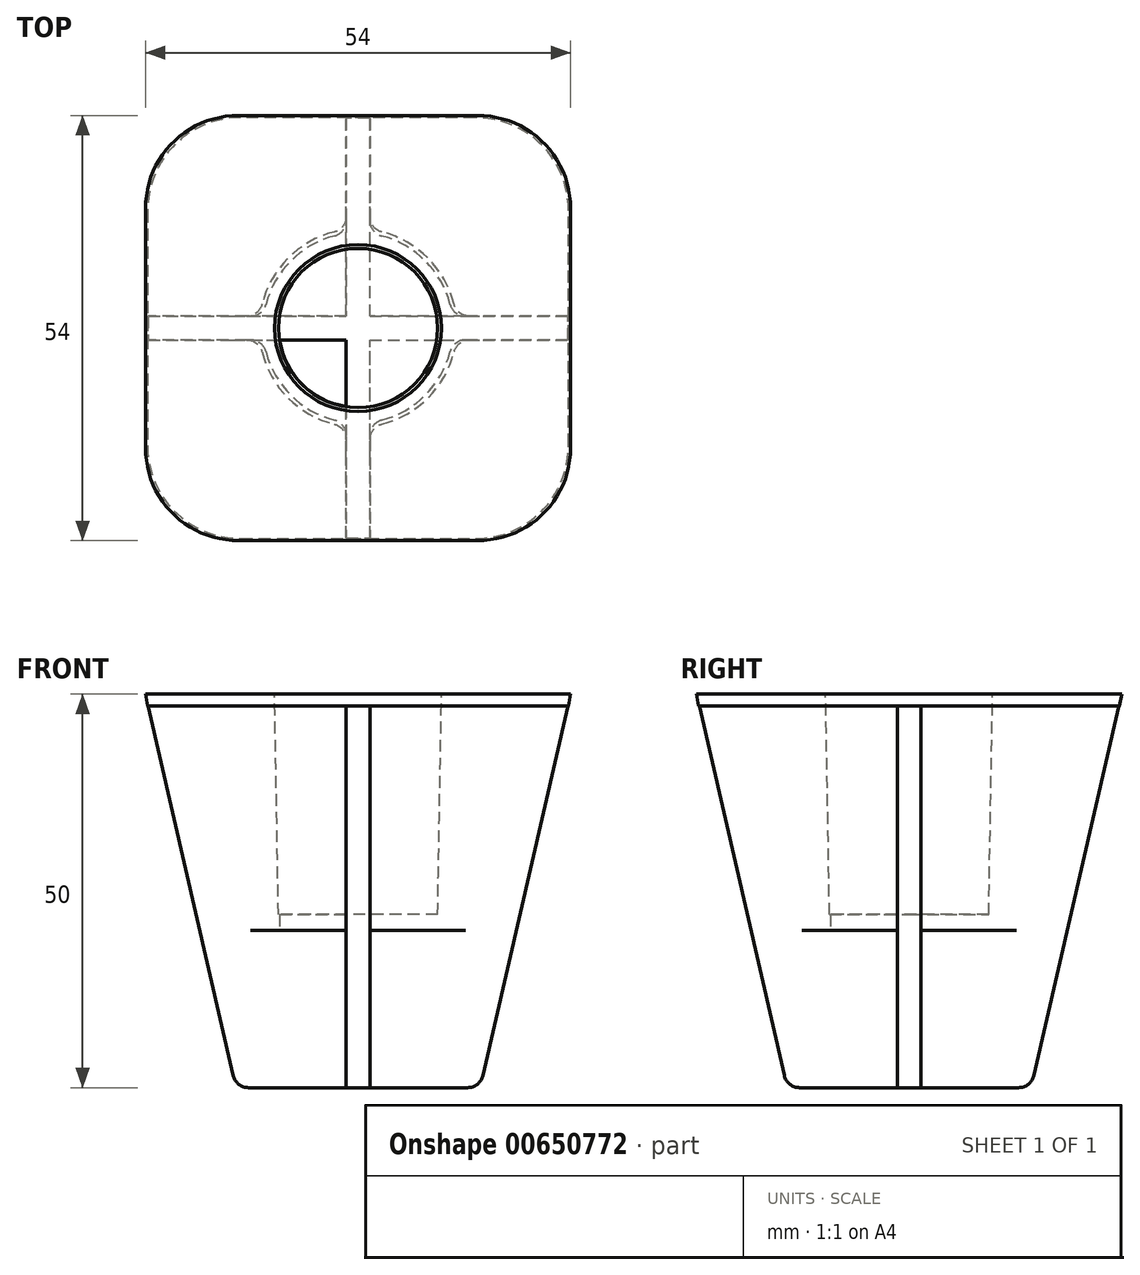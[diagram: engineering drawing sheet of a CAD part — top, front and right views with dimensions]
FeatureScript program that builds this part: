
annotation { "Feature Type Name" : "Feature", "Feature Type Description" : "" }
export const myFeature = defineFeature(function(context is Context, id is Id, definition is map)
    precondition{}
    {
        {
            var Q0;
            Q0=qCreatedBy(makeId("Top.planeOp"),FACE);
            var sketch = newSketch(context, id + "F0", { "sketchPlane" : qUnion([Q0])});
            skCircle(sketch, "E0", {"center": v(0, 0) * mm, "radius": 10.6 * mm});
            skSolve(sketch);
        }
        {
            var Q0;
            Q0 = qSketchRegion(id + "F0", true);
            extrude(context, id + "F1", {"entities" : qUnion([Q0]), "oppositeDirection" : true, "depth" : 28 * mm, "offsetDistance" : 25 * mm, "hasDraft" : true, "draftAngle" : 1 * degree, "draftPullDirection" : true});
        }
        {
            var Q0;
            Q0=makeQuery(id+"F1.opExtrude","CAP_FACE",FACE,{"disambiguationData":[OSD([sQuery(id+"F0.wireOp",EDGE,"E0")])],"isStart":true});
            shell(context, id + "F2", {"entities" : qUnion([Q0]), "thickness" : 2 * mm, "oppositeDirection" : true});
        }
        {
            var Q0;
            Q0=qCreatedBy(makeId("Right.planeOp"),FACE);
            var sketch = newSketch(context, id + "F3", { "sketchPlane" : qUnion([Q0])});
            skLineSegment(sketch, "E1", {"start": v(-10.6, 0) * mm, "end": v(-27, 0) * mm});
            skLineSegment(sketch, "E2", {"start": v(-27, 0) * mm, "end": v(-15.5, -50) * mm});
            skLineSegment(sketch, "E3", {"start": v(-15.5, -50) * mm, "end": v(0, -50) * mm});
            skLineSegment(sketch, "E4", {"start": v(0, -50) * mm, "end": v(15.5, -50) * mm});
            skLineSegment(sketch, "E5", {"start": v(15.5, -50) * mm, "end": v(27, 0) * mm});
            skLineSegment(sketch, "E6", {"start": v(27, 0) * mm, "end": v(10.6, 0) * mm});
            skLineSegment(sketch, "E7", {"start": v(10.6, 0) * mm, "end": v(10.45, -30) * mm});
            skLineSegment(sketch, "E8", {"start": v(10.45, -30) * mm, "end": v(-10.5, -30) * mm});
            skLineSegment(sketch, "E9", {"start": v(-10.5, -30) * mm, "end": v(-10.6, 0) * mm});
            skLineSegment(sketch, "E10.0", {"start": v(-10.6, 0) * mm, "end": v(10.6, 0) * mm, "construction": true});
            skSolve(sketch);
        }
        {
            var Q0;
            Q0 = qSketchRegion(id + "F3", true);
            extrude(context, id + "F4", {"entities" : qUnion([Q0]), "operationType" : NewBodyOperationType.ADD, "depth" : 1.5 * mm, "offsetDistance" : 25 * mm, "hasSecondDirection" : true, "secondDirectionOppositeDirection" : true, "secondDirectionDepth" : 1.5 * mm});
        }
        {
            var Q0;
            Q0=makeQuery(id+"F1.opExtrude","SWEPT_BODY",BODY,{"disambiguationData":[OSD([sQuery(id+"F0.wireOp",EDGE,"E0")])]});
            var Q1;
            {var subQ0=sQuery(id+"F0.wireOp",EDGE,"E0");Q1=makeQuery(id+"F2.opShell","OFFSET_FACE",FACE,{"disambiguationData":[OSD([subQ0]),TDD([makeQuery(id+"F1.opExtrude","SWEPT_FACE",FACE,{"disambiguationData":[OSD([subQ0])]})])]});}
            circularPattern(context, id + "F5", {"operationType" : NewBodyOperationType.ADD, "entities" : qUnion([Q0]), "axis" : qUnion([Q1]), "angle" : 360 * degree, "instanceCount" : 4, "equalSpace" : true});
        }
        {
            var Q0;
            {var subQ0=sQuery(id+"F0.wireOp",EDGE,"E0");var subQ2=sQuery(id+"F3.wireOp",EDGE,"E9");var subQ3=sQuery(id+"F3.wireOp",EDGE,"E8");var subQ4=sQuery(id+"F3.wireOp",EDGE,"E7");var subQ5=sQuery(id+"F3.wireOp",EDGE,"E6");var subQ6=sQuery(id+"F3.wireOp",EDGE,"E5");var subQ7=sQuery(id+"F3.wireOp",EDGE,"E4");var subQ8=sQuery(id+"F3.wireOp",EDGE,"E3");var subQ9=sQuery(id+"F3.wireOp",EDGE,"E2");var subQ10=sQuery(id+"F3.wireOp",EDGE,"E1");var subQ11=makeQuery(id+"F4.opExtrude","CAP_FACE",FACE,{"disambiguationData":[OSD([subQ10,subQ9,subQ8,subQ7,subQ6,subQ5,subQ4,subQ3,subQ2])],"isStart":true});Q0=makeQuery(id+"F5.boolean.opBoolean","SPLIT",FACE,{"disambiguationData":[TD([makeQuery(id+"F5.opPattern","COPY",FACE,{"derivedFrom":makeQuery(id+"F4.opExtrude","CAP_FACE",FACE,{"disambiguationData":[OSD([subQ10,subQ9,subQ8,subQ7,subQ6,subQ5,subQ4,subQ3,subQ2])],"isStart":false}),"instanceName":"1"})])],"derivedFrom":makeQuery(id+"F4.boolean.opBoolean","SPLIT",FACE,{"disambiguationData":[TD([subQ11])],"derivedFrom":makeQuery(id+"F1.opExtrude","CAP_FACE",FACE,{"disambiguationData":[OSD([subQ0])],"isStart":false})})});}
            var sketch = newSketch(context, id + "F6", { "sketchPlane" : qUnion([Q0])});
            skLineSegment(sketch, "E11.0", {"start": v(-9.96, 1.5) * mm, "end": v(-1.5, 1.5) * mm});
            skLineSegment(sketch, "E11.1", {"start": v(-1.5, 1.5) * mm, "end": v(-1.5, 9.96) * mm});
            skArc(sketch, "E12.0", {"start": v(-11.98, 1.5) * mm, "mid": v(-8.54, 8.54) * mm, "end": v(-1.5, 11.98) * mm, "construction": true});
            skArc(sketch, "E13.0", {"start": v(-9.96, 1.5) * mm, "mid": v(-7.13, 7.13) * mm, "end": v(-1.5, 9.96) * mm});
            skSolve(sketch);
        }
        {
            var Q0;
            Q0=makeQuery(id+"F6.imprint","IMPRINT",FACE,{"disambiguationData":[TD([[makeQuery(id+"F6.imprint","IMPRINT",EDGE,{"derivedFrom":sQuery(id+"F6.wireOp",EDGE,"E11.0")}),1.0]])]});
            extrude(context, id + "F7", {"entities" : qUnion([Q0]), "operationType" : NewBodyOperationType.REMOVE, "endBound" : BoundingType.UP_TO_NEXT, "oppositeDirection" : true, "depth" : 25 * mm, "offsetDistance" : 25 * mm});
        }
        {
            var Q0;
            Q0=makeQuery(id+"F4.opExtrude","SWEPT_EDGE",EDGE,{"disambiguationData":[OSD([sQuery(id+"F3.wireOp",EDGE,"E4"),sQuery(id+"F3.wireOp",EDGE,"E5")])]});
            var Q1;
            Q1=makeQuery(id+"F5.opPattern","COPY",EDGE,{"derivedFrom":makeQuery(id+"F4.opExtrude","SWEPT_EDGE",EDGE,{"disambiguationData":[OSD([sQuery(id+"F3.wireOp",EDGE,"E2"),sQuery(id+"F3.wireOp",EDGE,"E3")])]}),"instanceName":"1"});
            var Q2;
            Q2=makeQuery(id+"F5.opPattern","COPY",EDGE,{"derivedFrom":makeQuery(id+"F4.opExtrude","SWEPT_EDGE",EDGE,{"disambiguationData":[OSD([sQuery(id+"F3.wireOp",EDGE,"E4"),sQuery(id+"F3.wireOp",EDGE,"E5")])]}),"instanceName":"1"});
            var Q3;
            Q3=makeQuery(id+"F4.opExtrude","SWEPT_EDGE",EDGE,{"disambiguationData":[OSD([sQuery(id+"F3.wireOp",EDGE,"E2"),sQuery(id+"F3.wireOp",EDGE,"E3")])]});
            var Q4;
            Q4=makeQuery(id+"F5.opPattern","COPY",EDGE,{"derivedFrom":makeQuery(id+"F4.boolean.opBoolean","INTERSECT",EDGE,{"disambiguationData":[OD(1.0)],"derivedFrom":[makeQuery(id+"F1.opExtrude","SWEPT_FACE",FACE,{"disambiguationData":[OSD([sQuery(id+"F0.wireOp",EDGE,"E0")])]}),makeQuery(id+"F4.opExtrude","CAP_FACE",FACE,{"disambiguationData":[OSD([sQuery(id+"F3.wireOp",EDGE,"E1"),sQuery(id+"F3.wireOp",EDGE,"E2"),sQuery(id+"F3.wireOp",EDGE,"E3"),sQuery(id+"F3.wireOp",EDGE,"E4"),sQuery(id+"F3.wireOp",EDGE,"E5"),sQuery(id+"F3.wireOp",EDGE,"E6"),sQuery(id+"F3.wireOp",EDGE,"E7"),sQuery(id+"F3.wireOp",EDGE,"E8"),sQuery(id+"F3.wireOp",EDGE,"E9")])],"isStart":false})]}),"instanceName":"1"});
            var Q5;
            Q5=makeQuery(id+"F4.boolean.opBoolean","INTERSECT",EDGE,{"disambiguationData":[OD(0.0)],"derivedFrom":[makeQuery(id+"F1.opExtrude","SWEPT_FACE",FACE,{"disambiguationData":[OSD([sQuery(id+"F0.wireOp",EDGE,"E0")])]}),makeQuery(id+"F4.opExtrude","CAP_FACE",FACE,{"disambiguationData":[OSD([sQuery(id+"F3.wireOp",EDGE,"E1"),sQuery(id+"F3.wireOp",EDGE,"E2"),sQuery(id+"F3.wireOp",EDGE,"E3"),sQuery(id+"F3.wireOp",EDGE,"E4"),sQuery(id+"F3.wireOp",EDGE,"E5"),sQuery(id+"F3.wireOp",EDGE,"E6"),sQuery(id+"F3.wireOp",EDGE,"E7"),sQuery(id+"F3.wireOp",EDGE,"E8"),sQuery(id+"F3.wireOp",EDGE,"E9")])],"isStart":false})]});
            var Q6;
            Q6=makeQuery(id+"F5.opPattern","COPY",EDGE,{"derivedFrom":makeQuery(id+"F4.boolean.opBoolean","INTERSECT",EDGE,{"disambiguationData":[OD(0.0)],"derivedFrom":[makeQuery(id+"F1.opExtrude","SWEPT_FACE",FACE,{"disambiguationData":[OSD([sQuery(id+"F0.wireOp",EDGE,"E0")])]}),makeQuery(id+"F4.opExtrude","CAP_FACE",FACE,{"disambiguationData":[OSD([sQuery(id+"F3.wireOp",EDGE,"E1"),sQuery(id+"F3.wireOp",EDGE,"E2"),sQuery(id+"F3.wireOp",EDGE,"E3"),sQuery(id+"F3.wireOp",EDGE,"E4"),sQuery(id+"F3.wireOp",EDGE,"E5"),sQuery(id+"F3.wireOp",EDGE,"E6"),sQuery(id+"F3.wireOp",EDGE,"E7"),sQuery(id+"F3.wireOp",EDGE,"E8"),sQuery(id+"F3.wireOp",EDGE,"E9")])],"isStart":false})]}),"instanceName":"1"});
            var Q7;
            Q7=makeQuery(id+"F4.boolean.opBoolean","INTERSECT",EDGE,{"disambiguationData":[OD(1.0)],"derivedFrom":[makeQuery(id+"F1.opExtrude","SWEPT_FACE",FACE,{"disambiguationData":[OSD([sQuery(id+"F0.wireOp",EDGE,"E0")])]}),makeQuery(id+"F4.opExtrude","CAP_FACE",FACE,{"disambiguationData":[OSD([sQuery(id+"F3.wireOp",EDGE,"E1"),sQuery(id+"F3.wireOp",EDGE,"E2"),sQuery(id+"F3.wireOp",EDGE,"E3"),sQuery(id+"F3.wireOp",EDGE,"E4"),sQuery(id+"F3.wireOp",EDGE,"E5"),sQuery(id+"F3.wireOp",EDGE,"E6"),sQuery(id+"F3.wireOp",EDGE,"E7"),sQuery(id+"F3.wireOp",EDGE,"E8"),sQuery(id+"F3.wireOp",EDGE,"E9")])],"isStart":false})]});
            var Q8;
            Q8=makeQuery(id+"F5.opPattern","COPY",EDGE,{"derivedFrom":makeQuery(id+"F4.boolean.opBoolean","INTERSECT",EDGE,{"disambiguationData":[OD(0.0)],"derivedFrom":[makeQuery(id+"F1.opExtrude","SWEPT_FACE",FACE,{"disambiguationData":[OSD([sQuery(id+"F0.wireOp",EDGE,"E0")])]}),makeQuery(id+"F4.opExtrude","CAP_FACE",FACE,{"disambiguationData":[OSD([sQuery(id+"F3.wireOp",EDGE,"E1"),sQuery(id+"F3.wireOp",EDGE,"E2"),sQuery(id+"F3.wireOp",EDGE,"E3"),sQuery(id+"F3.wireOp",EDGE,"E4"),sQuery(id+"F3.wireOp",EDGE,"E5"),sQuery(id+"F3.wireOp",EDGE,"E6"),sQuery(id+"F3.wireOp",EDGE,"E7"),sQuery(id+"F3.wireOp",EDGE,"E8"),sQuery(id+"F3.wireOp",EDGE,"E9")])],"isStart":true})]}),"instanceName":"1"});
            var Q9;
            Q9=makeQuery(id+"F4.boolean.opBoolean","INTERSECT",EDGE,{"disambiguationData":[OD(0.0)],"derivedFrom":[makeQuery(id+"F1.opExtrude","SWEPT_FACE",FACE,{"disambiguationData":[OSD([sQuery(id+"F0.wireOp",EDGE,"E0")])]}),makeQuery(id+"F4.opExtrude","CAP_FACE",FACE,{"disambiguationData":[OSD([sQuery(id+"F3.wireOp",EDGE,"E1"),sQuery(id+"F3.wireOp",EDGE,"E2"),sQuery(id+"F3.wireOp",EDGE,"E3"),sQuery(id+"F3.wireOp",EDGE,"E4"),sQuery(id+"F3.wireOp",EDGE,"E5"),sQuery(id+"F3.wireOp",EDGE,"E6"),sQuery(id+"F3.wireOp",EDGE,"E7"),sQuery(id+"F3.wireOp",EDGE,"E8"),sQuery(id+"F3.wireOp",EDGE,"E9")])],"isStart":true})]});
            var Q10;
            Q10=makeQuery(id+"F5.opPattern","COPY",EDGE,{"derivedFrom":makeQuery(id+"F4.boolean.opBoolean","INTERSECT",EDGE,{"disambiguationData":[OD(1.0)],"derivedFrom":[makeQuery(id+"F1.opExtrude","SWEPT_FACE",FACE,{"disambiguationData":[OSD([sQuery(id+"F0.wireOp",EDGE,"E0")])]}),makeQuery(id+"F4.opExtrude","CAP_FACE",FACE,{"disambiguationData":[OSD([sQuery(id+"F3.wireOp",EDGE,"E1"),sQuery(id+"F3.wireOp",EDGE,"E2"),sQuery(id+"F3.wireOp",EDGE,"E3"),sQuery(id+"F3.wireOp",EDGE,"E4"),sQuery(id+"F3.wireOp",EDGE,"E5"),sQuery(id+"F3.wireOp",EDGE,"E6"),sQuery(id+"F3.wireOp",EDGE,"E7"),sQuery(id+"F3.wireOp",EDGE,"E8"),sQuery(id+"F3.wireOp",EDGE,"E9")])],"isStart":true})]}),"instanceName":"1"});
            var Q11;
            Q11=makeQuery(id+"F4.boolean.opBoolean","INTERSECT",EDGE,{"disambiguationData":[OD(1.0)],"derivedFrom":[makeQuery(id+"F1.opExtrude","SWEPT_FACE",FACE,{"disambiguationData":[OSD([sQuery(id+"F0.wireOp",EDGE,"E0")])]}),makeQuery(id+"F4.opExtrude","CAP_FACE",FACE,{"disambiguationData":[OSD([sQuery(id+"F3.wireOp",EDGE,"E1"),sQuery(id+"F3.wireOp",EDGE,"E2"),sQuery(id+"F3.wireOp",EDGE,"E3"),sQuery(id+"F3.wireOp",EDGE,"E4"),sQuery(id+"F3.wireOp",EDGE,"E5"),sQuery(id+"F3.wireOp",EDGE,"E6"),sQuery(id+"F3.wireOp",EDGE,"E7"),sQuery(id+"F3.wireOp",EDGE,"E8"),sQuery(id+"F3.wireOp",EDGE,"E9")])],"isStart":true})]});
            fillet(context, id + "F8", {"entities" : qUnion([Q0, Q1, Q2, Q3, Q4, Q5, Q6, Q7, Q8, Q9, Q10, Q11]), "radius" : 2 * mm, "tangentPropagation" : true, "allowEdgeOverflow" : false});
        }
        {
            var Q0;
            {var subQ0=makeQuery(id+"F4.boolean.opBoolean","MERGE",FACE,{"derivedFrom":[makeQuery(id+"F1.opExtrude","CAP_FACE",FACE,{"disambiguationData":[OSD([sQuery(id+"F0.wireOp",EDGE,"E0")])],"isStart":true}),makeQuery(id+"F4.opExtrude","SWEPT_FACE",FACE,{"disambiguationData":[OSD([sQuery(id+"F3.wireOp",EDGE,"E1")])]}),makeQuery(id+"F4.opExtrude","SWEPT_FACE",FACE,{"disambiguationData":[OSD([sQuery(id+"F3.wireOp",EDGE,"E6")])]})]});Q0=makeQuery(id+"F5.boolean.opBoolean","MERGE",FACE,{"derivedFrom":[subQ0,makeQuery(id+"F5.opPattern","COPY",FACE,{"derivedFrom":subQ0,"instanceName":"1"}),makeQuery(id+"F5.opPattern","COPY",FACE,{"derivedFrom":subQ0,"instanceName":"2"}),makeQuery(id+"F5.opPattern","COPY",FACE,{"derivedFrom":subQ0,"instanceName":"3"})]});}
            var sketch = newSketch(context, id + "F9", { "sketchPlane" : qUnion([Q0])});
            skLineSegment(sketch, "E14.bottom", {"start": v(27, -27) * mm, "end": v(-27, -27) * mm});
            skLineSegment(sketch, "E14.top", {"start": v(27, 27) * mm, "end": v(-27, 27) * mm});
            skLineSegment(sketch, "E14.left", {"start": v(27, -27) * mm, "end": v(27, 27) * mm});
            skLineSegment(sketch, "E14.right", {"start": v(-27, -27) * mm, "end": v(-27, 27) * mm});
            skPoint(sketch, "E14.middle", {"position": v(0, 0) * mm});
            skCircle(sketch, "E15", {"center": v(0, 0) * mm, "radius": 11.65 * mm});
            skSolve(sketch);
        }
        {
            var Q0;
            Q0 = qSketchRegion(id + "F9", true);
            extrude(context, id + "F10", {"entities" : qUnion([Q0]), "operationType" : NewBodyOperationType.ADD, "oppositeDirection" : true, "depth" : 1.5 * mm, "offsetDistance" : 25 * mm, "hasDraft" : true, "draftAngle" : 10 * degree, "draftPullDirection" : true});
        }
        {
            var Q0;
            Q0=makeQuery(id+"F10.opExtrude","SWEPT_EDGE",EDGE,{"disambiguationData":[OSD([sQuery(id+"F9.wireOp",EDGE,"E14.bottom"),sQuery(id+"F9.wireOp",EDGE,"E14.left")])]});
            var Q1;
            Q1=makeQuery(id+"F10.opExtrude","SWEPT_EDGE",EDGE,{"disambiguationData":[OSD([sQuery(id+"F9.wireOp",EDGE,"E14.bottom"),sQuery(id+"F9.wireOp",EDGE,"E14.right")])]});
            var Q2;
            Q2=makeQuery(id+"F10.opExtrude","SWEPT_EDGE",EDGE,{"disambiguationData":[OSD([sQuery(id+"F9.wireOp",EDGE,"E14.top"),sQuery(id+"F9.wireOp",EDGE,"E14.right")])]});
            var Q3;
            Q3=makeQuery(id+"F10.opExtrude","SWEPT_EDGE",EDGE,{"disambiguationData":[OSD([sQuery(id+"F9.wireOp",EDGE,"E14.top"),sQuery(id+"F9.wireOp",EDGE,"E14.left")])]});
            fillet(context, id + "F11", {"entities" : qUnion([Q0, Q1, Q2, Q3]), "radius" : 12 * mm, "tangentPropagation" : true, "allowEdgeOverflow" : false});
        }
    });
